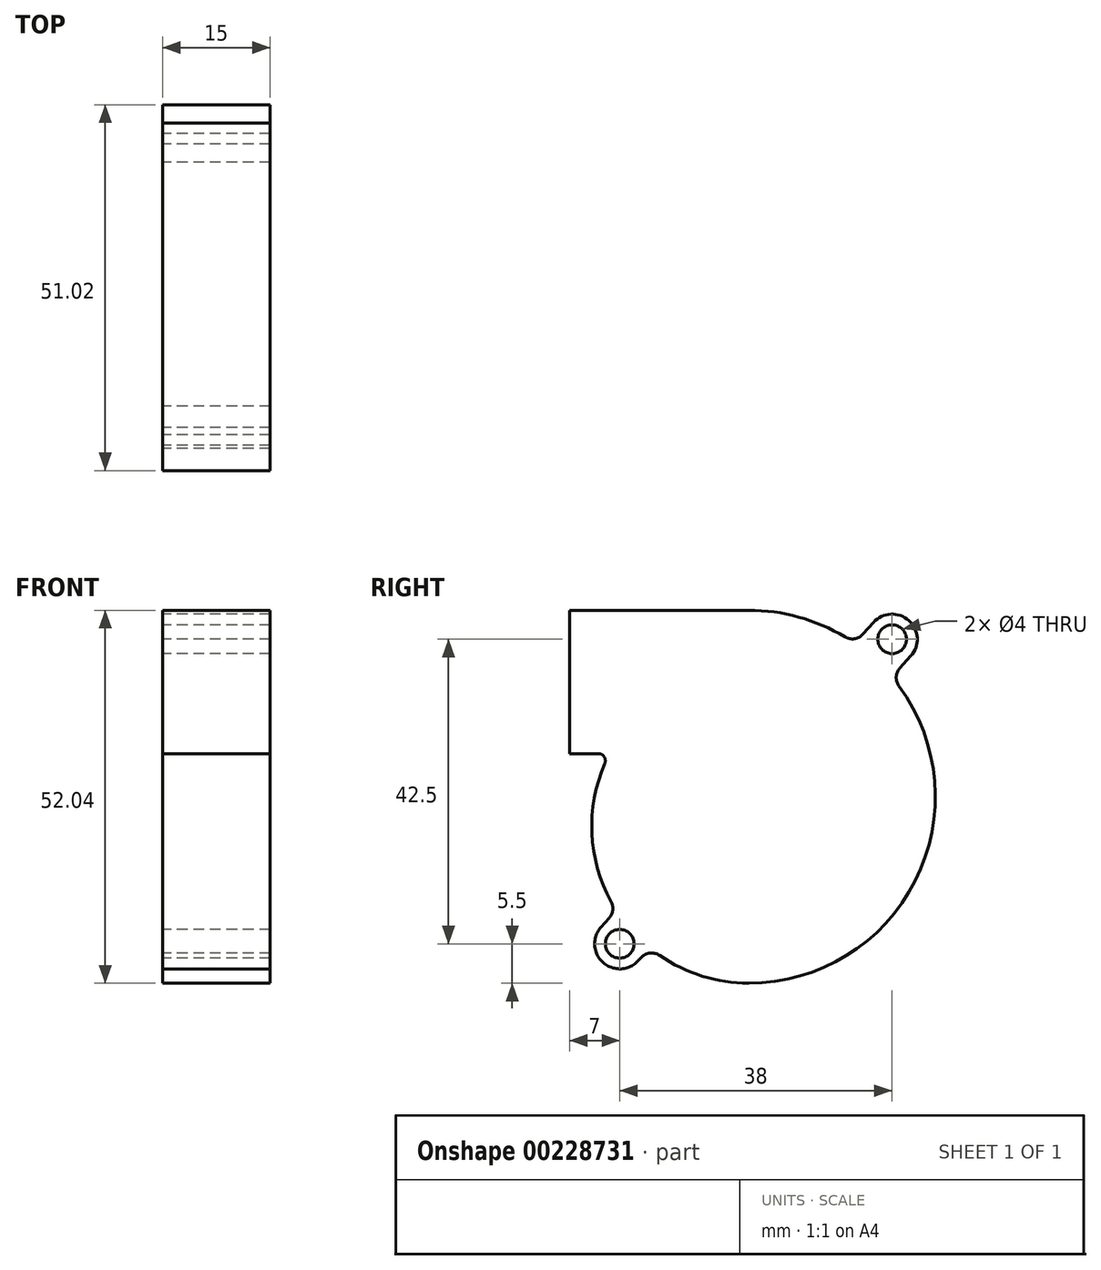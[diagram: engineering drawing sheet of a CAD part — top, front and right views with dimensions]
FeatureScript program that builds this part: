
annotation { "Feature Type Name" : "Feature", "Feature Type Description" : "" }
export const myFeature = defineFeature(function(context is Context, id is Id, definition is map)
    precondition{}
    {
        {
            var Q0;
            Q0=qCreatedBy(makeId("Right.planeOp"),FACE);
            var sketch = newSketch(context, id + "F0", { "sketchPlane" : qUnion([Q0])});
            skCircle(sketch, "E0", {"center": v(0, 0) * mm, "radius": 12 * mm});
            skCircle(sketch, "E1", {"center": v(20, 23) * mm, "radius": 2 * mm});
            skCircle(sketch, "E2", {"center": v(-18, -19.5) * mm, "radius": 2 * mm});
            skLineSegment(sketch, "E3", {"start": v(-25, 27.04) * mm, "end": v(-25, 7.04) * mm});
            skLineSegment(sketch, "E4", {"start": v(26, 45.4) * mm, "end": v(26, -37.85) * mm, "construction": true});
            skCircle(sketch, "E5", {"center": v(0, 0) * mm, "radius": 16 * mm});
            skLineSegment(sketch, "E6", {"start": v(-25, 27.04) * mm, "end": v(65.28, 27.04) * mm, "construction": true});
            skLineSegment(sketch, "E7", {"start": v(-25, 27.04) * mm, "end": v(0, 27.04) * mm});
            skArc(sketch, "E8", {"start": v(22.6, 20.66) * mm, "mid": v(22.34, 25.6) * mm, "end": v(17.4, 25.34) * mm});
            skArc(sketch, "E9", {"start": v(-20.6, -17.16) * mm, "mid": v(-20.34, -22.1) * mm, "end": v(-15.4, -21.84) * mm});
            skArc(sketch, "E10", {"start": v(26, 0) * mm, "mid": v(24.88, 8.65) * mm, "end": v(20.95, 16.45) * mm});
            skArc(sketch, "E11", {"start": v(0, -25) * mm, "mid": v(18.03, -17.74) * mm, "end": v(26, 0) * mm});
            skArc(sketch, "E12", {"start": v(-20.08, 5.64) * mm, "mid": v(-21.88, -4.09) * mm, "end": v(-19.21, -13.62) * mm});
            skLineSegment(sketch, "E13", {"start": v(-25, 7.04) * mm, "end": v(-21, 7.04) * mm});
            skPoint(sketch, "E14.visualSharp", {"position": v(-19.41, 7.04) * mm});
            skArc(sketch, "E14.filletArc", {"start": v(-20.08, 5.64) * mm, "mid": v(-20.16, 6.59) * mm, "end": v(-21, 7.04) * mm});
            skLineSegment(sketch, "E15", {"start": v(-20.6, -17.16) * mm, "end": v(-19.48, -15.91) * mm});
            skLineSegment(sketch, "E16", {"start": v(-15.4, -21.84) * mm, "end": v(-15.04, -21.45) * mm});
            skLineSegment(sketch, "E17", {"start": v(17.4, 25.34) * mm, "end": v(15.92, 23.7) * mm});
            skLineSegment(sketch, "E18", {"start": v(22.6, 20.66) * mm, "end": v(21.08, 18.97) * mm});
            skArc(sketch, "E19.trimOffspring", {"start": v(-12.42, -21.14) * mm, "mid": v(-6.5, -24.01) * mm, "end": v(0, -25) * mm});
            skArc(sketch, "E20.trimOffspring", {"start": v(13.4, 23.32) * mm, "mid": v(6.95, 26.1) * mm, "end": v(0, 27.04) * mm});
            skPoint(sketch, "E21.visualSharp", {"position": v(14.78, 22.44) * mm});
            skArc(sketch, "E21.filletArc", {"start": v(13.4, 23.32) * mm, "mid": v(14.73, 23.06) * mm, "end": v(15.92, 23.7) * mm});
            skPoint(sketch, "E22.visualSharp", {"position": v(19.95, 17.72) * mm});
            skArc(sketch, "E22.filletArc", {"start": v(21.08, 18.97) * mm, "mid": v(20.57, 17.73) * mm, "end": v(20.95, 16.45) * mm});
            skPoint(sketch, "E23.visualSharp", {"position": v(-18.5, -14.82) * mm});
            skArc(sketch, "E23.filletArc", {"start": v(-19.48, -15.91) * mm, "mid": v(-18.98, -14.8) * mm, "end": v(-19.21, -13.62) * mm});
            skPoint(sketch, "E24.visualSharp", {"position": v(-13.82, -20.09) * mm});
            skArc(sketch, "E24.filletArc", {"start": v(-12.42, -21.14) * mm, "mid": v(-13.79, -20.8) * mm, "end": v(-15.04, -21.45) * mm});
            skSolve(sketch);
        }
        {
            var Q0;
            Q0=makeQuery(id+"F0.imprint","IMPRINT",FACE,{"disambiguationData":[TD([[makeQuery(id+"F0.imprint","IMPRINT",EDGE,{"derivedFrom":sQuery(id+"F0.wireOp",EDGE,"E1")}),-1.0]])]});
            var Q1;
            Q1=makeQuery(id+"F0.imprint","IMPRINT",FACE,{"disambiguationData":[TD([[makeQuery(id+"F0.imprint","IMPRINT",EDGE,{"derivedFrom":sQuery(id+"F0.wireOp",EDGE,"E0")}),-1.0]])]});
            var Q2;
            Q2=makeQuery(id+"F0.imprint","IMPRINT",FACE,{"disambiguationData":[TD([[makeQuery(id+"F0.imprint","IMPRINT",EDGE,{"derivedFrom":sQuery(id+"F0.wireOp",EDGE,"E0")}),1.0]])]});
            extrude(context, id + "F1", {"entities" : qUnion([Q0, Q1, Q2]), "depth" : 15 * mm});
        }
    });
